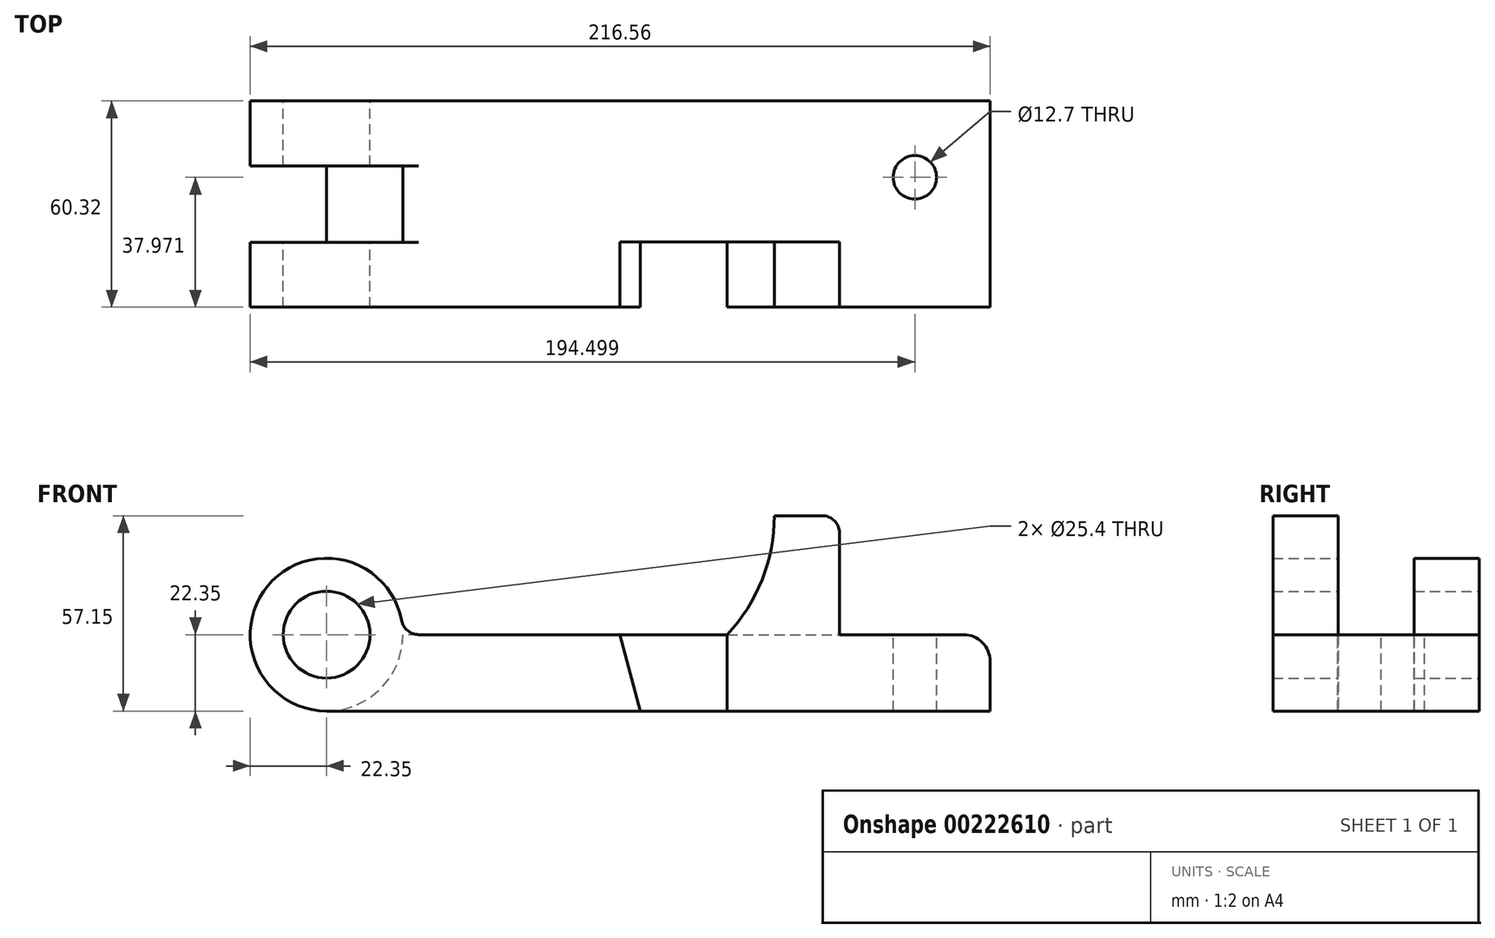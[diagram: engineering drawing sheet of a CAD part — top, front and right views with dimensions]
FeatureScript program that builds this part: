
annotation { "Feature Type Name" : "Feature", "Feature Type Description" : "" }
export const myFeature = defineFeature(function(context is Context, id is Id, definition is map)
    precondition{}
    {
        {
            var Q0;
            Q0=qCreatedBy(makeId("Front.planeOp"),FACE);
            var sketch = newSketch(context, id + "F0", { "sketchPlane" : qUnion([Q0])});
            skCircle(sketch, "E0", {"center": v(0, 0) * mm, "radius": 12.7 * mm});
            skCircle(sketch, "E1", {"center": v(0, 0) * mm, "radius": 22.35 * mm});
            skLineSegment(sketch, "E2", {"start": v(22.35, 0) * mm, "end": v(194.2, 0) * mm});
            skLineSegment(sketch, "E3", {"start": v(0, -22.35) * mm, "end": v(194.2, -22.35) * mm});
            skLineSegment(sketch, "E4", {"start": v(194.2, -22.35) * mm, "end": v(194.2, 0) * mm});
            skLineSegment(sketch, "E5", {"start": v(117.25, 0) * mm, "end": v(117.25, -22.35) * mm});
            skLineSegment(sketch, "E6", {"start": v(85.85, 0) * mm, "end": v(91.85, -22.35) * mm});
            skLineSegment(sketch, "E7", {"start": v(150.09, 0) * mm, "end": v(150.09, 34.8) * mm});
            skLineSegment(sketch, "E8", {"start": v(150.09, 34.8) * mm, "end": v(131.04, 34.8) * mm});
            skArc(sketch, "E9", {"start": v(131.04, 34.8) * mm, "mid": v(127.46, 16.08) * mm, "end": v(117.25, 0) * mm});
            skSolve(sketch);
        }
        {
            var Q0;
            Q0=makeQuery(id+"F0.imprint","IMPRINT",FACE,{"disambiguationData":[TD([[makeQuery(id+"F0.imprint","IMPRINT",EDGE,{"derivedFrom":sQuery(id+"F0.wireOp",EDGE,"E0")}),-1.0]])]});
            var Q1;
            {var subQ5=sQuery(id+"F0.wireOp",EDGE,"E6");Q1=makeQuery(id+"F0.imprint","IMPRINT",FACE,{"disambiguationData":[TD([[makeQuery(id+"F0.imprint","IMPRINT",EDGE,{"derivedFrom":subQ5}),-1.0]])]});}
            var Q2;
            {var subQ0=sQuery(id+"F0.wireOp",EDGE,"E5");Q2=makeQuery(id+"F0.imprint","IMPRINT",FACE,{"disambiguationData":[TD([[makeQuery(id+"F0.imprint","IMPRINT",EDGE,{"derivedFrom":subQ0}),-1.0]])]});}
            var Q3;
            {var subQ0=sQuery(id+"F0.wireOp",EDGE,"E4");Q3=makeQuery(id+"F0.imprint","IMPRINT",FACE,{"disambiguationData":[TD([[makeQuery(id+"F0.imprint","IMPRINT",EDGE,{"derivedFrom":subQ0}),1.0]])]});}
            extrude(context, id + "F1", {"entities" : qUnion([Q0, Q1, Q2, Q3]), "endBound" : BoundingType.SYMMETRIC, "depth" : 60.32 * mm});
        }
        {
            var Q0;
            Q0=makeQuery(id+"F0.imprint","IMPRINT",FACE,{"disambiguationData":[TD([[makeQuery(id+"F0.imprint","IMPRINT",EDGE,{"derivedFrom":sQuery(id+"F0.wireOp",EDGE,"E0")}),-1.0]])]});
            extrude(context, id + "F2", {"entities" : qUnion([Q0]), "operationType" : NewBodyOperationType.REMOVE, "endBound" : BoundingType.SYMMETRIC, "oppositeDirection" : true, "depth" : 22.33 * mm});
        }
        {
            var Q0;
            Q0=makeQuery(id+"F1.opExtrude","CAP_FACE",FACE,{"disambiguationData":[OSD([sQuery(id+"F0.wireOp",EDGE,"E0"),sQuery(id+"F0.wireOp",EDGE,"E1"),sQuery(id+"F0.wireOp",EDGE,"E2"),sQuery(id+"F0.wireOp",EDGE,"E3"),sQuery(id+"F0.wireOp",EDGE,"E4")])],"isStart":false});
            var sketch = newSketch(context, id + "F3", { "sketchPlane" : qUnion([Q0])});
            skPoint(sketch, "E10.0", {"position": v(88.85, -11.18) * mm});
            skLineSegment(sketch, "E11.0", {"start": v(85.85, 0) * mm, "end": v(91.85, -22.35) * mm});
            skLineSegment(sketch, "E12.0", {"start": v(117.25, 0) * mm, "end": v(117.25, -22.35) * mm});
            skLineSegment(sketch, "E13.0.0", {"start": v(117.25, 0) * mm, "end": v(150.09, 0) * mm});
            skLineSegment(sketch, "E13.0.1", {"start": v(150.09, 0) * mm, "end": v(150.09, 34.8) * mm});
            skLineSegment(sketch, "E13.0.2", {"start": v(150.09, 34.8) * mm, "end": v(131.04, 34.8) * mm});
            skArc(sketch, "E13.0.3", {"start": v(131.04, 34.8) * mm, "mid": v(127.46, 16.08) * mm, "end": v(117.25, 0) * mm});
            skLineSegment(sketch, "E14", {"start": v(117.25, 0) * mm, "end": v(85.85, 0) * mm});
            skLineSegment(sketch, "E15", {"start": v(91.85, -22.35) * mm, "end": v(117.25, -22.35) * mm});
            skSolve(sketch);
        }
        {
            var Q0;
            Q0=makeQuery(id+"F3.imprint","IMPRINT",FACE,{"disambiguationData":[TD([[makeQuery(id+"F3.imprint","IMPRINT",EDGE,{"derivedFrom":sQuery(id+"F3.wireOp",EDGE,"E11.0")}),1.0]])]});
            extrude(context, id + "F4", {"entities" : qUnion([Q0]), "operationType" : NewBodyOperationType.REMOVE, "oppositeDirection" : true, "depth" : 19.05 * mm});
        }
        {
            var Q0;
            Q0=makeQuery(id+"F3.imprint","IMPRINT",FACE,{"disambiguationData":[TD([[makeQuery(id+"F3.imprint","IMPRINT",EDGE,{"derivedFrom":sQuery(id+"F3.wireOp",EDGE,"E13.0.0")}),1.0]])]});
            extrude(context, id + "F5", {"entities" : qUnion([Q0]), "operationType" : NewBodyOperationType.ADD, "oppositeDirection" : true, "depth" : 19.05 * mm});
        }
        {
            var Q0;
            Q0=makeQuery(id+"F1.opExtrude","SWEPT_FACE",FACE,{"disambiguationData":[OSD([sQuery(id+"F0.wireOp",EDGE,"E2")])]});
            var sketch = newSketch(context, id + "F6", { "sketchPlane" : qUnion([Q0])});
            skCircle(sketch, "E16", {"center": v(172.15, 7.81) * mm, "radius": 6.35 * mm});
            skPoint(sketch, "E16.centerSnap0", {"position": v(172.15, -30.16) * mm});
            skSolve(sketch);
        }
        {
            var Q0;
            Q0 = qSketchRegion(id + "F6", true);
            extrude(context, id + "F7", {"entities" : qUnion([Q0]), "operationType" : NewBodyOperationType.REMOVE, "endBound" : BoundingType.THROUGH_ALL, "oppositeDirection" : true, "depth" : 25.4 * mm});
        }
        {
            var Q0;
            Q0=makeQuery(id+"F1.opExtrude","SWEPT_EDGE",EDGE,{"disambiguationData":[OSD([sQuery(id+"F0.wireOp",EDGE,"E2"),sQuery(id+"F0.wireOp",EDGE,"E4")])]});
            fillet(context, id + "F8", {"entities" : qUnion([Q0]), "radius" : 7.87 * mm, "tangentPropagation" : true, "allowEdgeOverflow" : false});
        }
        {
            var Q0;
            Q0=makeQuery(id+"F5.opExtrude","SWEPT_EDGE",EDGE,{"disambiguationData":[OSD([sQuery(id+"F3.wireOp",EDGE,"E13.0.1"),sQuery(id+"F3.wireOp",EDGE,"E13.0.2")])]});
            fillet(context, id + "F9", {"entities" : qUnion([Q0]), "radius" : 5.08 * mm, "tangentPropagation" : true, "allowEdgeOverflow" : false});
        }
        {
            var Q0;
            {var subQ0=sQuery(id+"F0.wireOp",EDGE,"E1");var subQ1=sQuery(id+"F0.wireOp",EDGE,"E0");var subQ2=sQuery(id+"F0.wireOp",EDGE,"E2");Q0=makeQuery(id+"F2.boolean.opBoolean","SPLIT",EDGE,{"disambiguationData":[TD([makeQuery(id+"F1.opExtrude","CAP_FACE",FACE,{"disambiguationData":[OSD([subQ1,subQ0,subQ2,sQuery(id+"F0.wireOp",EDGE,"E3"),sQuery(id+"F0.wireOp",EDGE,"E4")])],"isStart":false}),makeQuery(id+"F1.opExtrude","SWEPT_FACE",FACE,{"disambiguationData":[OSD([subQ0])]}),makeQuery(id+"F1.opExtrude","SWEPT_FACE",FACE,{"disambiguationData":[OSD([subQ2])]}),makeQuery(id+"F2.opExtrude","CAP_FACE",FACE,{"disambiguationData":[OSD([subQ1,subQ0])],"isStart":true}),makeQuery(id+"F2.opExtrude","SWEPT_FACE",FACE,{"disambiguationData":[OSD([subQ0])]})])],"derivedFrom":makeQuery(id+"F1.opExtrude","SWEPT_EDGE",EDGE,{"disambiguationData":[OSD([subQ0,subQ2])]})});}
            var Q1;
            {var subQ0=sQuery(id+"F0.wireOp",EDGE,"E1");var subQ1=sQuery(id+"F0.wireOp",EDGE,"E0");var subQ2=sQuery(id+"F0.wireOp",EDGE,"E2");Q1=makeQuery(id+"F2.boolean.opBoolean","SPLIT",EDGE,{"disambiguationData":[TD([makeQuery(id+"F1.opExtrude","CAP_FACE",FACE,{"disambiguationData":[OSD([subQ1,subQ0,subQ2,sQuery(id+"F0.wireOp",EDGE,"E3"),sQuery(id+"F0.wireOp",EDGE,"E4")])],"isStart":true}),makeQuery(id+"F1.opExtrude","SWEPT_FACE",FACE,{"disambiguationData":[OSD([subQ0])]}),makeQuery(id+"F1.opExtrude","SWEPT_FACE",FACE,{"disambiguationData":[OSD([subQ2])]}),makeQuery(id+"F2.opExtrude","CAP_FACE",FACE,{"disambiguationData":[OSD([subQ1,subQ0])],"isStart":false}),makeQuery(id+"F2.opExtrude","SWEPT_FACE",FACE,{"disambiguationData":[OSD([subQ0])]})])],"derivedFrom":makeQuery(id+"F1.opExtrude","SWEPT_EDGE",EDGE,{"disambiguationData":[OSD([subQ0,subQ2])]})});}
            var Q2;
            Q2=makeQuery(id+"F5.opExtrude","SWEPT_EDGE",EDGE,{"disambiguationData":[OSD([sQuery(id+"F0.wireOp",EDGE,"E2"),sQuery(id+"F3.wireOp",EDGE,"E13.0.0"),sQuery(id+"F3.wireOp",EDGE,"E13.0.1")])]});
            fillet(context, id + "F10", {"entities" : qUnion([Q0, Q1, Q2]), "radius" : 5.08 * mm, "tangentPropagation" : true, "allowEdgeOverflow" : false});
        }
    });
